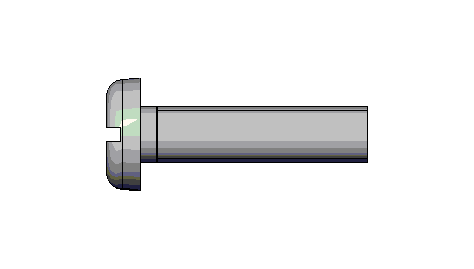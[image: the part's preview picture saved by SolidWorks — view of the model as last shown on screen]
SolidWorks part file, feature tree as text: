
SOLIDWORKS PART (.sldprt)
format: sldprt  version: not decoded by parser v0  size: 123,392 bytes
history: native  units: mm
features: plane x3, sketch x3, fillet x2, revolve x1, thread x1, cut_extrude x1, cut_revolve x1, pattern_linear x1 (+8 scaffold rows collapsed; 1 parser-record rows omitted)
feature tree (22):
  scaffold x8  (default folders/planes/origin — collapsed)
  plane  "Plane1"
  plane  "Plane2"
  plane  "Plane3"
  parser-record x1  (decoder bookkeeping rows leaked as tree rows — omitted from the tree; the rows remain in map.json)
  revolve  "Base-Revolve"  [1 undecoded]
  sketch  "BodySke"  dims[c1.Head_fillet_rad=3.6322mm c1.D1=~7.099516mm c1.Head_ang=85.0deg c1.Oval_ht=2.3876mm c1.Head_ht=6.1976mm c1.Diameter=9.525mm c1.Length=76.2mm c1.Head_dia=20.0152mm c2.Head_dia=15.3924mm c2.Head_ht=8.509mm c2.Length=40.0mm c2.Head_side_ht=6.1722mm c3.Head_ht=6.0mm c3.Head_dia=18.4912mm c3.Advance=1.5mm c3.Thread_nom=40.0mm c3.Thread_lim=36.5125mm c4.Head_dia=20.0mm c4.D2=152.4mm c4.Head_side_angle=5.0deg c4.Diameter=10.0mm]
  thread  "ThreadCosmetic"  Diameter=37mm Thread_length=37mm Thread_minor=8.377mm  [1 undecoded]
  fillet  "Fillet1"  Radius=0.4mm Head_dia=20mm Diameter=10mm
  fillet  "Fillet2"  Radius=3mm
  sketch  "Sketch2"  dims[D1=20.0mm Slot_width=2.5mm D2=10.0mm D3=1.25mm]
  cut_extrude  "Slot"  Depth=2.4mm Slot_depth=2.4mm
  sketch  "ThdSchSke"  dims[c1.Thread_minor=~1.03886mm c1.Diameter=~1.413535mm c1.Start=~0.988134mm c1.D4=~4.446753mm c1.Vee=60.0deg c2.Thread_minor=~1.03886mm c2.Start=~2.540025mm c2.D1=~0.108159mm c2.D2=~0.108159mm c3.D1=~0.216319mm c3.SideAngle=55.0deg c3.D2=~0.216319mm c3.VeeAngle=70.0deg c3.Thread_minor=8.377mm c3.Overcut=12.5mm c3.Diameter=10.0mm c3.D6=~8.326268mm c4.D1=~8.326268mm c5.D1=90.0deg c5.Start=11.1125mm c6.Start=~44.450025mm c7.Start=9.0mm]
  cut_revolve  "ThreadSchematic"  Angle=360deg
  pattern_linear  "ThdSchPat"  Count1=26 Count2=1 Spacing1=1.48mm Spacing2=50mm Num_threads=26 Advance=1.48mm
decode coverage: 9 of 10 modeling features carry decoded parameters
note: ~ marks probable driven/reference dimensions
note: 2 parameter values undecoded
note: suppression state not decoded; provenance and decode notes live in map.json
